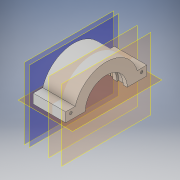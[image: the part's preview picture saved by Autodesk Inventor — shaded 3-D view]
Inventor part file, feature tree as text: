
AUTODESK INVENTOR PART (.ipt)
format: ipt  version: 2019 (Build 230136000, 136)  size: 563,200 bytes
history: native  units: mm
features: sketch x27, extrude x22, mirror x13, plane x12, projected_geometry x12, other x4, fillet x4, hole x3
ambient origin geometry x8: Origin, YZ Plane, XZ Plane, XY Plane, X Axis, Y Axis, Z Axis, Center Point
bodies: Body1 (feature_tree)
feature tree (97):
  other  "實體1"
  extrude  "擠出1"  Depth=123.43mm
  plane  "工作平面2"
  extrude  "擠出3"  Depth=160.0mm
  plane  "工作平面3"
  extrude  "擠出4"  Depth=120.0mm TaperAngle=0.0deg
  extrude  "擠出5"  [1 undecoded]
  plane  "工作平面4"
  extrude  "擠出7"  Depth=130.0mm
  plane  "工作平面5"
  extrude  "擠出9"  Depth=15.0mm TaperAngle=0.0deg
  extrude  "擠出10"  [1 undecoded]
  extrude  "擠出11"  Depth=111.375mm
  extrude  "擠出12"  Depth=10.0mm TaperAngle=0.0deg
  mirror  "鏡射1"
  fillet  "圓角2"  Radius=10.0mm
  fillet  "圓角3"  Radius=10.0mm
  sketch  "草圖16"
  plane  "工作平面7"
  mirror  "鏡射2"
  fillet  "圓角5"  [1 undecoded]
  fillet  "圓角6"  Radius=10.0mm
  plane  "工作平面8"
  plane  "工作平面9"
  sketch  "草圖20"
  extrude  "擠出15"  [1 undecoded]
  plane  "工作平面10"
  extrude  "擠出16"  Depth=10.0mm
  extrude  "擠出17"  Depth=10.0mm TaperAngle=0.0deg
  plane  "工作平面11"
  extrude  "擠出19"  Depth=10.0mm TaperAngle=0.0deg
  extrude  "擠出20"  Depth=160.0mm
  mirror  "鏡射3"
  mirror  "鏡射4"
  extrude  "擠出21"  Depth=80.0mm
  mirror  "鏡射7"
  plane  "工作平面15"
  mirror  "鏡射9"
  hole  "孔2"  [1 undecoded]
  mirror  "鏡射10"
  mirror  "鏡射11"
  hole  "孔3"  [1 undecoded]
  mirror  "鏡射12"
  mirror  "鏡射13"
  extrude  "擠出22"  Depth=160.0mm
  extrude  "擠出23"  Depth=120.0mm TaperAngle=0.0deg
  extrude  "擠出24"  Depth=120.0mm TaperAngle=0.0deg
  extrude  "擠出25"  Depth=25.0mm
  extrude  "擠出27"  Depth=20.0mm
  extrude  "擠出28"  Depth=2.0mm
  mirror  "鏡射14"
  plane  "工作平面17"
  hole  "孔4"  [1 undecoded]
  mirror  "鏡射15"
  mirror  "鏡射16"
  other  "分割2"
  other  "分割3"
  other  "分割4"
  extrude  "擠出30"  Depth=40.0mm
  sketch  "草圖1"
  sketch  "草圖4"
  sketch  "草圖6"
  sketch  "草圖7"
  projected_geometry  "投影迴路1"
  sketch  "草圖9"
  projected_geometry  "投影迴路4"
  sketch  "草圖11"
  sketch  "草圖12"
  projected_geometry  "投影迴路6"
  sketch  "草圖13"
  projected_geometry  "投影迴路7"
  sketch  "草圖14"
  plane  "工作平面6"
  sketch  "草圖17"
  projected_geometry  "投影迴路8"
  sketch  "草圖24"
  projected_geometry  "投影迴路11"
  sketch  "草圖25"
  sketch  "草圖26"
  sketch  "草圖27"
  sketch  "草圖28"
  sketch  "草圖29"
  projected_geometry  "投影迴路12"
  sketch  "草圖30"
  sketch  "草圖31"
  sketch  "草圖32"
  projected_geometry  "投影迴路13"
  projected_geometry  "投影迴路14"
  projected_geometry  "投影迴路15"
  sketch  "草圖33"
  sketch  "草圖34"
  sketch  "草圖35"
  projected_geometry  "投影迴路16"
  sketch  "草圖36"
  sketch  "草圖37"
  sketch  "草圖38"
  projected_geometry  "投影迴路17"
note: 7 required parameter values undecoded (feature->parameter linkage not recoverable at this tier; creation-order binding heuristic only, values carry confidence <= 0.55)
